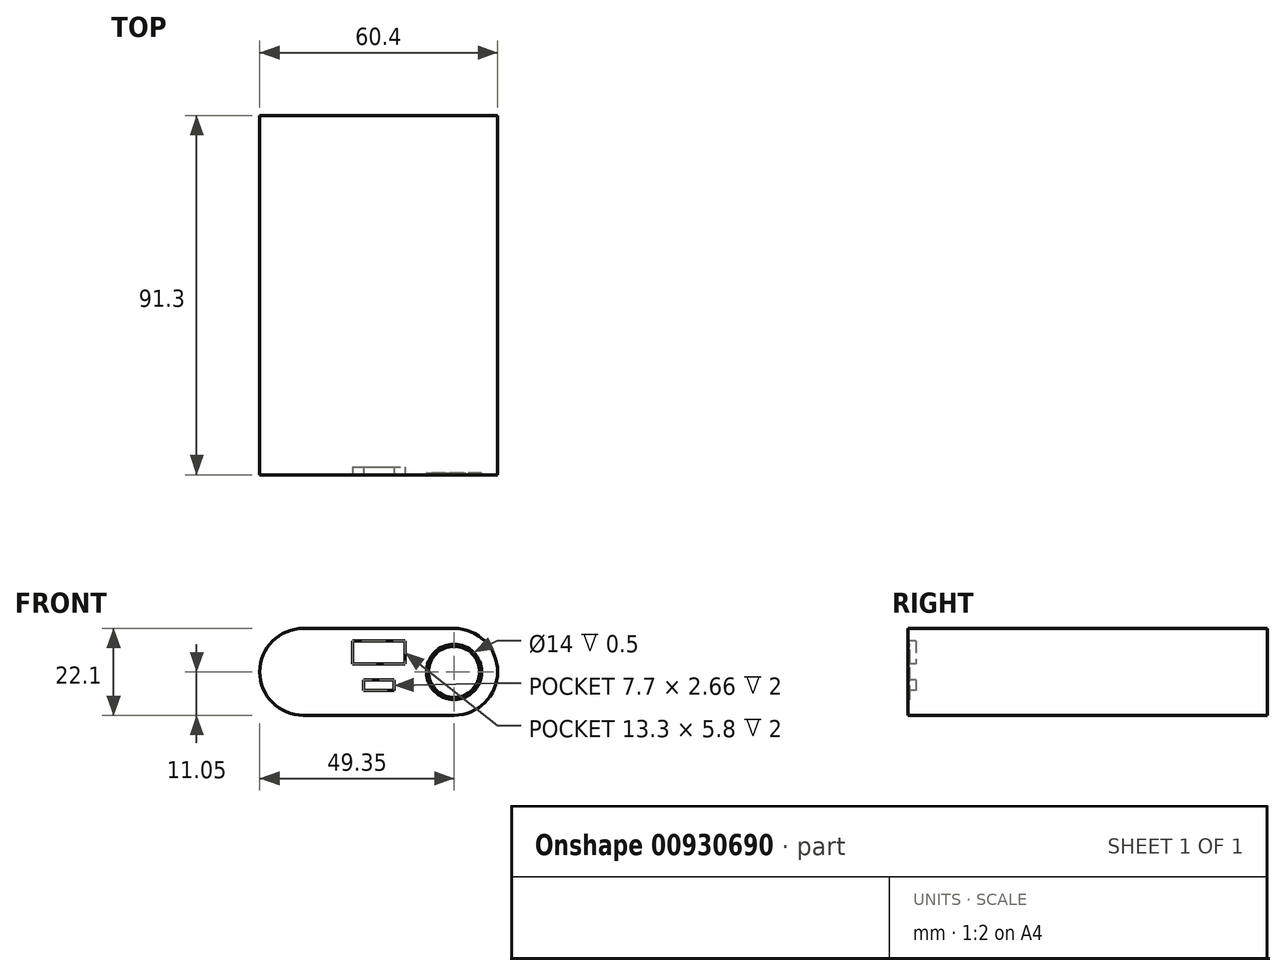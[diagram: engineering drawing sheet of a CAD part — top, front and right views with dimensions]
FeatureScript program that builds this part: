
annotation { "Feature Type Name" : "Feature", "Feature Type Description" : "" }
export const myFeature = defineFeature(function(context is Context, id is Id, definition is map)
    precondition{}
    {
        {
            var Q0;
            Q0=qCreatedBy(makeId("Front.planeOp"),FACE);
            var sketch = newSketch(context, id + "F0", { "sketchPlane" : qUnion([Q0])});
            skLineSegment(sketch, "E0.bottom", {"start": v(11.05, 22.1) * mm, "end": v(49.35, 22.1) * mm});
            skLineSegment(sketch, "E0.top", {"start": v(11.05, 0) * mm, "end": v(49.35, 0) * mm});
            skArc(sketch, "E1", {"start": v(11.05, 22.1) * mm, "mid": v(0, 11.05) * mm, "end": v(11.05, 0) * mm});
            skArc(sketch, "E2", {"start": v(49.35, 0) * mm, "mid": v(60.4, 11.05) * mm, "end": v(49.35, 22.1) * mm});
            skSolve(sketch);
        }
        {
            var Q0;
            Q0=qSketchRegion(id+"F0",true);
            extrude(context, id + "F1", {"entities" : qUnion([Q0]), "depth" : 91.3 * mm});
        }
        {
            var Q0;
            Q0=makeQuery(id+"F1.opExtrude","CAP_FACE",FACE,{"disambiguationData":[OSD([sQuery(id+"F0.wireOp",EDGE,"E0.bottom"),sQuery(id+"F0.wireOp",EDGE,"E0.top"),sQuery(id+"F0.wireOp",EDGE,"E1"),sQuery(id+"F0.wireOp",EDGE,"E2")])],"isStart":false});
            var sketch = newSketch(context, id + "F2", { "sketchPlane" : qUnion([Q0])});
            skLineSegment(sketch, "E3.bottom", {"start": v(23.55, 18.9) * mm, "end": v(36.85, 18.9) * mm});
            skLineSegment(sketch, "E3.top", {"start": v(23.55, 13.1) * mm, "end": v(36.85, 13.1) * mm});
            skLineSegment(sketch, "E3.left", {"start": v(23.55, 18.9) * mm, "end": v(23.55, 13.1) * mm});
            skLineSegment(sketch, "E3.right", {"start": v(36.85, 18.9) * mm, "end": v(36.85, 13.1) * mm});
            skLineSegment(sketch, "E4.bottom", {"start": v(26.35, 8.96) * mm, "end": v(34.05, 8.96) * mm});
            skLineSegment(sketch, "E4.top", {"start": v(26.35, 6.3) * mm, "end": v(34.05, 6.3) * mm});
            skLineSegment(sketch, "E4.left", {"start": v(26.35, 8.96) * mm, "end": v(26.35, 6.3) * mm});
            skLineSegment(sketch, "E4.right", {"start": v(34.05, 8.96) * mm, "end": v(34.05, 6.3) * mm});
            skLineSegment(sketch, "E5", {"start": v(30.2, 22.1) * mm, "end": v(30.2, 0) * mm, "construction": true});
            skSolve(sketch);
        }
        {
            var Q0;
            Q0=qSketchRegion(id+"F2",true);
            extrude(context, id + "F3", {"entities" : qUnion([Q0]), "operationType" : NewBodyOperationType.REMOVE, "oppositeDirection" : true, "depth" : 2 * mm});
        }
        {
            var Q0;
            Q0=makeQuery(id+"F1.opExtrude","CAP_FACE",FACE,{"disambiguationData":[OSD([sQuery(id+"F0.wireOp",EDGE,"E0.bottom"),sQuery(id+"F0.wireOp",EDGE,"E0.top"),sQuery(id+"F0.wireOp",EDGE,"E1"),sQuery(id+"F0.wireOp",EDGE,"E2")])],"isStart":false});
            var sketch = newSketch(context, id + "F4", { "sketchPlane" : qUnion([Q0])});
            skCircle(sketch, "E6", {"center": v(49.35, 11.05) * mm, "radius": 7 * mm});
            skCircle(sketch, "E7", {"center": v(49.35, 11.05) * mm, "radius": 6.5 * mm});
            skSolve(sketch);
        }
        {
            var Q0;
            Q0=qSketchRegion(id+"F4",true);
            extrude(context, id + "F5", {"entities" : qUnion([Q0]), "operationType" : NewBodyOperationType.REMOVE, "oppositeDirection" : true, "depth" : 0.5 * mm});
        }
    });
